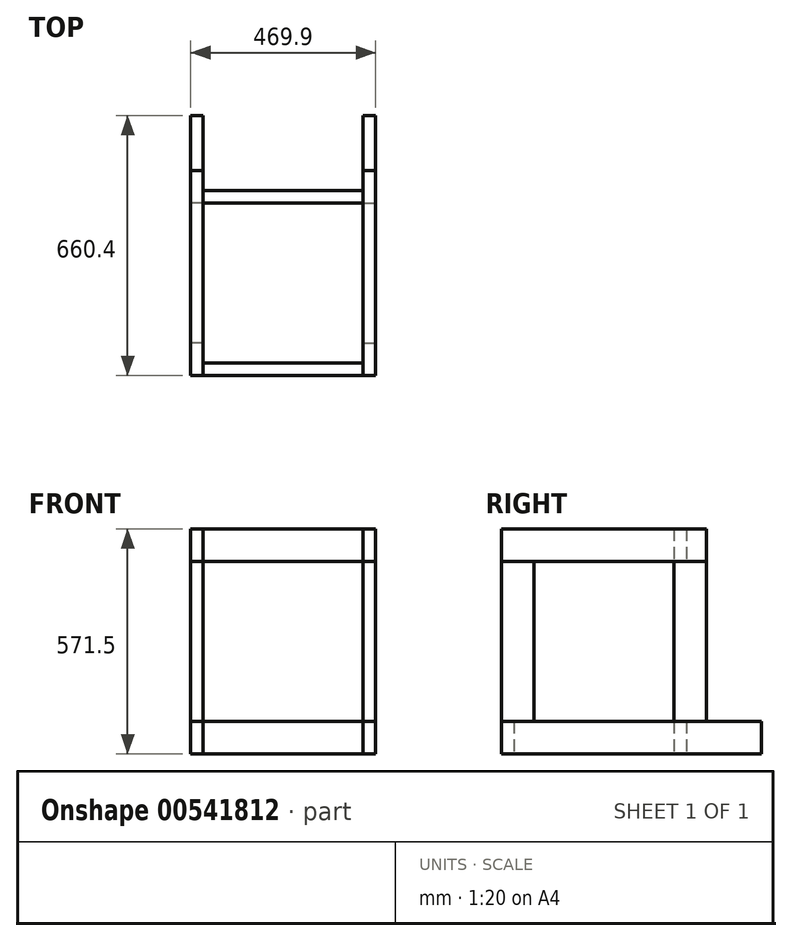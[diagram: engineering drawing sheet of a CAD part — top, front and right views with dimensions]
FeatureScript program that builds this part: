
annotation { "Feature Type Name" : "Feature", "Feature Type Description" : "" }
export const myFeature = defineFeature(function(context is Context, id is Id, definition is map)
    precondition{}
    {
        {
            var Q0;
            Q0=qCreatedBy(makeId("Top.planeOp"),FACE);
            var sketch = newSketch(context, id + "F0", { "sketchPlane" : qUnion([Q0])});
            skLineSegment(sketch, "E0.top", {"start": v(-203.2, -203.2) * mm, "end": v(203.2, -203.2) * mm});
            skLineSegment(sketch, "E0.left", {"start": v(-203.2, -234.95) * mm, "end": v(-203.2, -203.2) * mm});
            skLineSegment(sketch, "E0.right", {"start": v(203.2, -234.95) * mm, "end": v(203.2, -203.2) * mm});
            skLineSegment(sketch, "E1", {"start": v(0, 266.7) * mm, "end": v(0, -199.6) * mm, "construction": true});
            skLineSegment(sketch, "E2", {"start": v(-203.2, -234.95) * mm, "end": v(203.2, -234.95) * mm});
            skLineSegment(sketch, "E3", {"start": v(-150.67, 0) * mm, "end": v(236.67, 0) * mm, "construction": true});
            skLineSegment(sketch, "E4.MirrorCS", {"start": v(-203.2, 234.95) * mm, "end": v(203.2, 234.95) * mm});
            skLineSegment(sketch, "E5.MirrorCS", {"start": v(203.2, 234.95) * mm, "end": v(203.2, 203.2) * mm});
            skLineSegment(sketch, "E6.MirrorCS", {"start": v(-203.2, 203.2) * mm, "end": v(203.2, 203.2) * mm});
            skLineSegment(sketch, "E7.MirrorCS", {"start": v(-203.2, 234.95) * mm, "end": v(-203.2, 203.2) * mm});
            skSolve(sketch);
        }
        {
            var Q0;
            Q0=makeQuery(id+"F0.imprint","IMPRINT",FACE,{"disambiguationData":[TD([[makeQuery(id+"F0.imprint","IMPRINT",EDGE,{"derivedFrom":sQuery(id+"F0.wireOp",EDGE,"E4.MirrorCS")}),-1.0]])]});
            var Q1;
            Q1=makeQuery(id+"F0.imprint","IMPRINT",FACE,{"disambiguationData":[TD([[makeQuery(id+"F0.imprint","IMPRINT",EDGE,{"derivedFrom":sQuery(id+"F0.wireOp",EDGE,"E0.top")}),-1.0]])]});
            extrude(context, id + "F1", {"entities" : qUnion([Q0, Q1]), "depth" : 82.55 * mm, "offsetDistance" : 25.4 * mm});
        }
        {
            var Q0;
            Q0=qCreatedBy(makeId("Top.planeOp"),FACE);
            var sketch = newSketch(context, id + "F2", { "sketchPlane" : qUnion([Q0])});
            skLineSegment(sketch, "E8.bottom", {"start": v(-234.95, 425.45) * mm, "end": v(-203.2, 425.45) * mm});
            skLineSegment(sketch, "E8.top", {"start": v(-234.95, -234.95) * mm, "end": v(-203.2, -234.95) * mm});
            skLineSegment(sketch, "E8.left", {"start": v(-234.95, 425.45) * mm, "end": v(-234.95, -234.95) * mm});
            skLineSegment(sketch, "E8.right", {"start": v(-203.2, 425.45) * mm, "end": v(-203.2, -234.95) * mm});
            skLineSegment(sketch, "E9.bottom", {"start": v(203.2, 425.45) * mm, "end": v(234.95, 425.45) * mm});
            skLineSegment(sketch, "E9.top", {"start": v(203.2, -234.95) * mm, "end": v(234.95, -234.95) * mm});
            skLineSegment(sketch, "E9.left", {"start": v(203.2, 425.45) * mm, "end": v(203.2, -234.95) * mm});
            skLineSegment(sketch, "E9.right", {"start": v(234.95, 425.45) * mm, "end": v(234.95, -234.95) * mm});
            skLineSegment(sketch, "E10", {"start": v(0, 0) * mm, "end": v(0, 572.26) * mm, "construction": true});
            skSolve(sketch);
        }
        {
            var Q0;
            Q0=makeQuery(id+"F2.imprint","IMPRINT",FACE,{"disambiguationData":[TD([[makeQuery(id+"F2.imprint","IMPRINT",EDGE,{"derivedFrom":sQuery(id+"F2.wireOp",EDGE,"E8.bottom")}),-1.0]])]});
            var Q1;
            Q1=makeQuery(id+"F2.imprint","IMPRINT",FACE,{"disambiguationData":[TD([[makeQuery(id+"F2.imprint","IMPRINT",EDGE,{"derivedFrom":sQuery(id+"F2.wireOp",EDGE,"E9.bottom")}),-1.0]])]});
            extrude(context, id + "F3", {"entities" : qUnion([Q0, Q1]), "depth" : 82.55 * mm, "offsetDistance" : 25.4 * mm});
        }
        {
            var Q0;
            Q0=makeQuery(id+"F3.opExtrude","SWEPT_FACE",FACE,{"disambiguationData":[OSD([sQuery(id+"F2.wireOp",EDGE,"E9.right")])]});
            var sketch = newSketch(context, id + "F4", { "sketchPlane" : qUnion([Q0])});
            skLineSegment(sketch, "E11.bottom", {"start": v(-234.95, 82.55) * mm, "end": v(-152.4, 82.55) * mm});
            skLineSegment(sketch, "E11.top", {"start": v(-234.95, 488.95) * mm, "end": v(-152.4, 488.95) * mm});
            skLineSegment(sketch, "E11.left", {"start": v(-234.95, 82.55) * mm, "end": v(-234.95, 488.95) * mm});
            skLineSegment(sketch, "E11.right", {"start": v(-152.4, 82.55) * mm, "end": v(-152.4, 488.95) * mm});
            skLineSegment(sketch, "E12.bottom", {"start": v(203.2, 82.55) * mm, "end": v(285.75, 82.55) * mm});
            skLineSegment(sketch, "E12.top", {"start": v(203.2, 488.95) * mm, "end": v(285.75, 488.95) * mm});
            skLineSegment(sketch, "E12.left", {"start": v(203.2, 82.55) * mm, "end": v(203.2, 488.95) * mm});
            skLineSegment(sketch, "E12.right", {"start": v(285.75, 82.55) * mm, "end": v(285.75, 488.95) * mm});
            skSolve(sketch);
        }
        {
            var Q0;
            Q0 = qSketchRegion(id + "F4", true);
            extrude(context, id + "F5", {"entities" : qUnion([Q0]), "oppositeDirection" : true, "depth" : 31.75 * mm, "offsetDistance" : 25.4 * mm});
        }
        {
            var Q0;
            Q0=makeQuery(id+"F5.opExtrude","CAP_FACE",FACE,{"disambiguationData":[OSD([sQuery(id+"F4.wireOp",EDGE,"E11.bottom"),sQuery(id+"F4.wireOp",EDGE,"E11.top"),sQuery(id+"F4.wireOp",EDGE,"E11.left"),sQuery(id+"F4.wireOp",EDGE,"E11.right")])],"isStart":true});
            var sketch = newSketch(context, id + "F6", { "sketchPlane" : qUnion([Q0])});
            skLineSegment(sketch, "E13.bottom", {"start": v(-234.95, 488.95) * mm, "end": v(285.75, 488.95) * mm});
            skLineSegment(sketch, "E13.top", {"start": v(-234.95, 571.5) * mm, "end": v(285.75, 571.5) * mm});
            skLineSegment(sketch, "E13.left", {"start": v(-234.95, 488.95) * mm, "end": v(-234.95, 571.5) * mm});
            skLineSegment(sketch, "E13.right", {"start": v(285.75, 488.95) * mm, "end": v(285.75, 571.5) * mm});
            skSolve(sketch);
        }
        {
            var Q0;
            Q0=makeQuery(id+"F6.imprint","IMPRINT",FACE,{"disambiguationData":[TD([[makeQuery(id+"F6.imprint","IMPRINT",EDGE,{"derivedFrom":sQuery(id+"F6.wireOp",EDGE,"E13.top")}),-1.0]])]});
            extrude(context, id + "F7", {"entities" : qUnion([Q0]), "oppositeDirection" : true, "depth" : 31.75 * mm, "offsetDistance" : 25.4 * mm});
        }
        {
            var Q0;
            Q0=makeQuery(id+"F5.opExtrude","SWEPT_BODY",BODY,{"disambiguationData":[OSD([sQuery(id+"F4.wireOp",EDGE,"E12.bottom"),sQuery(id+"F4.wireOp",EDGE,"E12.top"),sQuery(id+"F4.wireOp",EDGE,"E12.left"),sQuery(id+"F4.wireOp",EDGE,"E12.right")])]});
            var Q1;
            Q1=makeQuery(id+"F5.opExtrude","SWEPT_BODY",BODY,{"disambiguationData":[OSD([sQuery(id+"F4.wireOp",EDGE,"E11.bottom"),sQuery(id+"F4.wireOp",EDGE,"E11.top"),sQuery(id+"F4.wireOp",EDGE,"E11.left"),sQuery(id+"F4.wireOp",EDGE,"E11.right")])]});
            var Q2;
            Q2=makeQuery(id+"F7.opExtrude","SWEPT_BODY",BODY,{"disambiguationData":[OSD([sQuery(id+"F6.wireOp",EDGE,"E13.bottom"),sQuery(id+"F6.wireOp",EDGE,"E13.top"),sQuery(id+"F6.wireOp",EDGE,"E13.left"),sQuery(id+"F6.wireOp",EDGE,"E13.right")])]});
            var Q3;
            Q3=qCreatedBy(makeId("Right.planeOp"),FACE);
            mirror(context, id + "F8", {"entities" : qUnion([Q0, Q1, Q2]), "mirrorPlane" : qUnion([Q3])});
        }
        {
            var Q0;
            Q0=makeQuery(id+"F8.opPattern","COPY",FACE,{"derivedFrom":makeQuery(id+"F5.opExtrude","SWEPT_FACE",FACE,{"disambiguationData":[OSD([sQuery(id+"F4.wireOp",EDGE,"E12.left")])]}),"instanceName":"1"});
            var sketch = newSketch(context, id + "F9", { "sketchPlane" : qUnion([Q0])});
            skLineSegment(sketch, "E14.bottom", {"start": v(-203.2, 571.5) * mm, "end": v(203.2, 571.5) * mm});
            skLineSegment(sketch, "E14.top", {"start": v(-203.2, 488.95) * mm, "end": v(203.2, 488.95) * mm});
            skLineSegment(sketch, "E14.left", {"start": v(-203.2, 571.5) * mm, "end": v(-203.2, 488.95) * mm});
            skLineSegment(sketch, "E14.right", {"start": v(203.2, 571.5) * mm, "end": v(203.2, 488.95) * mm});
            skSolve(sketch);
        }
        {
            var Q0;
            Q0 = qSketchRegion(id + "F9", true);
            extrude(context, id + "F10", {"entities" : qUnion([Q0]), "oppositeDirection" : true, "depth" : 31.75 * mm, "offsetDistance" : 25.4 * mm});
        }
    });
